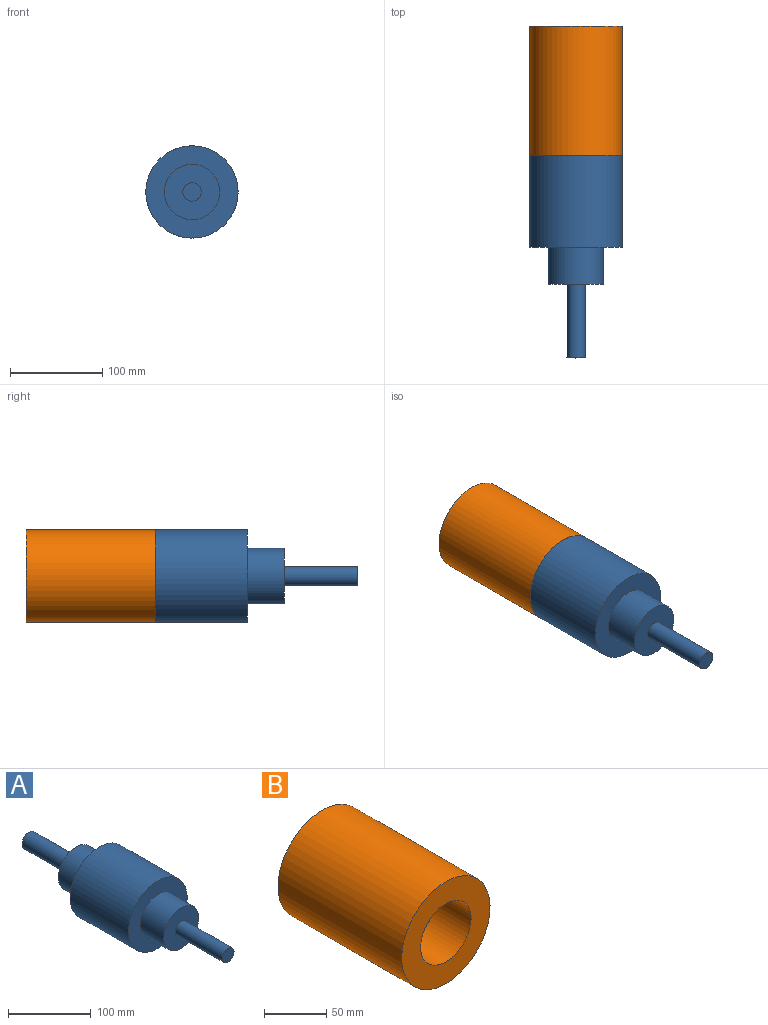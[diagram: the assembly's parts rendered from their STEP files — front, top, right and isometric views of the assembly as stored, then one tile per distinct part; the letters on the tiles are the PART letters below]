
ASSEMBLY  parts=2 mates=1
PART A: 11 faces, bbox 100x340x100 mm
  f0: cylinder r=50mm len=100mm, axis (0,1,0), area 31415.9mm2, adj f1,f2
  f1: plane 100x100mm, normal (0,1,0), area 5026.5mm2, adj f0,f7
  f2: plane 100x100mm, normal (0,-1,0), area 5026.5mm2, adj f0,f3
  f3: cylinder r=30mm len=60mm, axis (0,1,0), area 7539.8mm2, adj f2,f4
  f4: plane 60x60mm, normal (0,-1,0), area 2513.3mm2, adj f3,f5
  f5: cylinder r=10mm len=80mm, axis (0,1,0), area 5026.5mm2, adj f4,f6
  f6: plane 20x20mm, normal (0,-1,0), area 314.2mm2, adj f5
  f7: cylinder r=30mm len=60mm, axis (0,-1,0), area 7539.8mm2, adj f1,f8
  f8: plane 60x60mm, normal (0,1,0), area 2383.4mm2, adj f7,f9
  f9: cylinder r=11.89mm len=80mm, axis (0,-1,0), area 5976.2mm2, adj f8,f10
  f10: plane 23.78x23.78mm, normal (0,1,0), area 444.1mm2, adj f9
PART B: 7 faces, bbox 100x140x100 mm
  f0: cylinder r=50mm len=140mm, axis (0,1,0), area 43982.3mm2, adj f1,f2
  f1: plane 100x100mm, normal (0,-1,0), area 5293mm2, adj f0,f3
  f2: plane 100x100mm, normal (0,1,0), area 7854mm2, adj f0
  f3: cylinder r=28.55mm len=57.1mm, axis (0,-1,0), area 7175.8mm2, adj f1,f4
  f4: plane 57.1x57.1mm, normal (0,-1,0), area 2036.1mm2, adj f3,f5
  f5: cylinder r=12.93mm len=80mm, axis (0,-1,0), area 6497.3mm2, adj f4,f6
  f6: plane 25.85x25.85mm, normal (0,-1,0), area 524.9mm2, adj f5
PLACE A t=(-72.91,-215.23,80.43)mm
PLACE B t=(-72.91,-75.23,80.43)mm
MATE fastened B.f0 <-> A.f0  axis (0,-1,0) through (-72.91,-215.23,80.43)mm
